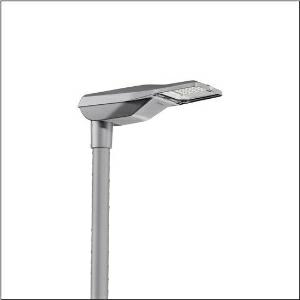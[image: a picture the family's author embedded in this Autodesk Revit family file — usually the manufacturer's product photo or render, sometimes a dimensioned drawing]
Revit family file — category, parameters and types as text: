
# Revit family: streetlight_sl_21_iq_micro___st1_0a_5xe1d61d08cb_4c5c
name_source: partatom
category: Lighting Fixtures
units: mm (PartAtom-declared; Revit-internal decimal feet)

## family parameters
Cut with Voids When Loaded = No
Host = Face
Light Source = No
Part Type = Normal
Room Calculation Point = No
Round Connector Dimension = Use Diameter
Shared = No

## types (1)
- --- (1 x LED, 2570 lm, 19.4 W, 2700K)
    Apparent Load = 19 VA
    CIE Flux Codes = 37 72 97 100 100
    Color Rendering = 70
    Color Temperature = 2700K
    Default Elevation = 1800 mm
    Description = Streetlight SL 21 iQ micro, mast luminaire, primary light control with lens, of PMMA, primary optical cover: cover, of toughened safety glass, transparent, light distribution: ST1.0a, light emission: direct distribution, primary light characteristic: asymmetric, installation type: post-top, side-entry, LED, High Power LED, rated luminous flux: 2.570lm, luminous efficacy: 133lm/W, light colour: 727, colour temperature: 2700K, control gear: iQ-Comfort, control: Auto-Match, Temp-Guard, Lumen-Switch, Night-Set, Smart-Wire, Light-Fading, Desk-Remote (wireless, voltage-free reading and setting of iQ features in the workshop via application-optimized NFC function/RFID function), optimised constant luminous flux control (CLO 2.0), pre-setting: linear dimming characteristic, mains connection: 220..240V, AC, 50/60Hz, start of lifetime: 19W, end of service life: 20W, reduction: 10W, luminaire housing, of diecast aluminium, powder-coated, SITECO metallic grey (DB 702S), corrosivity category C5 high according to DIN EN ISO 12944, please order mast flange separately, inclination adjustable: 0°, 5°, 10°, 15°, sealing non-destructively replaceable, multi-level sealing system, length: 528mm, width: 235mm, height: 110mm, mast flange for spigot size: 42mm (side-entry): 5XC10008XM4, 60/48mm (side-entry/post-top): 5XC10108XM2, 76/60mm (side-entry/post-top): 5XC10108XM1, protection rating (complete): IP66, insulation class (complete): insulation class II (safety insulation), certification: CE, ENEC, ENEC+, VDE, impact resistance: IK10, permissible operating ambient temperature for outdoor applications: -40..+50°C, standard-compliant lighting for roads and squares, packaging unit: 1 piece

Light Distribution: ST1.0a
    Height = 110 mm
    Lamp = 1 x LED
    Lamp Light Flux = 2570 lm
    Lamp Power = 19.4 W
    Lamp count = 1
    Length = 528 mm
    Luminous efficacy = 132 lm/W
    Manufacturer = Siteco
    ModVariant = No
    Model = 5XE1D61D08CB
    Number of Poles = 1
    OnlyDefault = Yes
    Power Factor = 1
    Product Name = Streetlight SL 21 iQ micro | ST1.0a
    Product group = mast luminaire | pylon top
    ProductGroupID = 6100
    Protection Class = Protection class II
    Protection Degree = IP 66
    RLX_Detail_Level = 1
    RLX_Emergency_Light_Flux = 0 lm
    RLX_Emergency_Type = 0
    RLX_Emergency_Type_DB = No
    RlxData = <blob elided: 99561 chars, md5=e7ffaec2>
    Socket = socket
    Standby Power = 0 W
    System Light Flux = 2570 lm
    System Power = 19 W
    Type Comments = factory setting: luminous flux: 100 % | dim-lin: 254 | 387 mA
    Type Image = l_1006881.jpg
    URL = http://relux.com
    VarID = @adj_138639
    Voltage = 0 V
    Weight = 0.00 kg
    Width = 235 mm

## geometry (parser evidence)
native form markers: Blend x4, Sweep x11
no freeform markers — native parametric forms only
